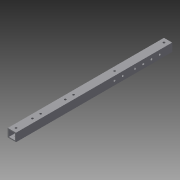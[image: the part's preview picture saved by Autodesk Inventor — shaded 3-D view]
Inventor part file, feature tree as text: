
AUTODESK INVENTOR PART (.ipt)
format: ipt  version: 2015 SP1 (Build 190203100, 203)  size: 160,768 bytes
history: native  units: in
note: dims shown in document units (in); Inventor stores cm internally (conversion verified against a paired STEP export)
features: sketch x7, hole x5, projected_geometry x3, extrude x2
ambient origin geometry x8: Origin, YZ Plane, XZ Plane, XY Plane, X Axis, Y Axis, Z Axis, Center Point
bodies: Solid1 (feature_tree)
feature tree (17):
  extrude  "Extrusion1"  Depth=1.0in
  sketch  "Sketch2"  dims[d2=0.75in d3=0.75in]
  hole  "Hole2"  [1 undecoded]
  hole  "Hole3"  [1 undecoded]
  hole  "Hole4"  [1 undecoded]
  extrude  "Extrusion2"  Depth=0.5in
  hole  "Hole6"  [1 undecoded]
  hole  "Hole7"  [1 undecoded]
  sketch  "Sketch1"  dims[d0=1.0in d1=1.0in]
  projected_geometry  "Projected Loop1"
  sketch  "Sketch3"  dims[d4=0.125in d5=0.125in]
  sketch  "Sketch4"  dims[d6=12.0in d7=0.0in d8=0.5in]
  projected_geometry  "Projected Loop2"
  sketch  "Sketch5"  dims[d9=0.5in d10=0.5in]
  sketch  "Sketch6"  dims[d11=0.5in d19=0.5in]
  sketch  "Sketch7"  dims[d20=0.5in d21=0.5in d22=1.5in d23=3.5in d24=2.5in d25=0.25in d26=0.75in d27=0.375in d28=0.25in d29=0.5635in d30=1.0in d31=0.8108in d32=0.5in d33=5.5in d34=0.25in d35=0.75in d36=0.375in d37=0.25in d38=0.5635in d39=1.0in d40=0.8108in d41=5.0in d42=7.5in d43=6.0in d44=0.5in d45=0.5in d46=0.5in d47=0.25in d48=0.75in d49=0.375in d50=0.25in d51=0.5635in d52=1.0in d53=0.8108in d54=7.0in d55=0.0in d56=0.5in d57=0.5in d65=2.5in d66=0.5in d67=0.25in d68=0.75in d69=0.375in d70=0.25in d71=0.5635in d72=1.0in d73=0.8108in d74=0.5in d75=0.5in d76=3.5in d77=6.5in d78=0.25in d79=0.75in d80=0.375in d81=0.25in d82=0.5635in d83=1.0in d84=0.8108in]
  projected_geometry  "Projected Loop3"
note: 5 required parameter values undecoded (feature->parameter linkage not recoverable at this tier; creation-order binding heuristic only, values carry confidence <= 0.55)
